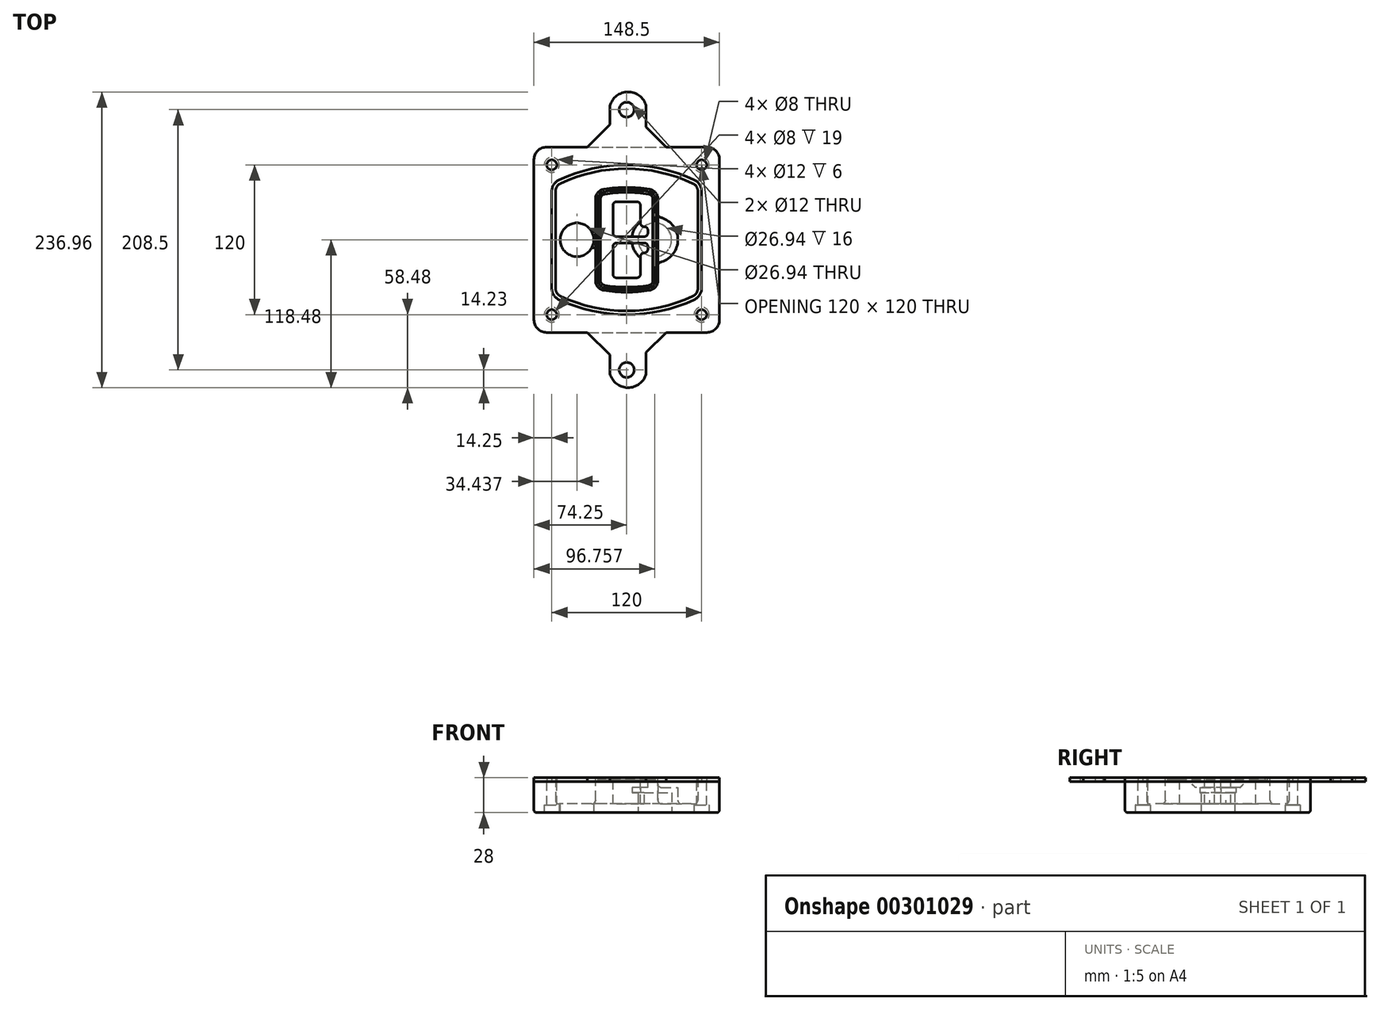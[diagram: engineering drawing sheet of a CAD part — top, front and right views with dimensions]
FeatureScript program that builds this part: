
annotation { "Feature Type Name" : "Feature", "Feature Type Description" : "" }
export const myFeature = defineFeature(function(context is Context, id is Id, definition is map)
    precondition{}
    {
        {
            var Q0;
            Q0=qCreatedBy(makeId("Top.planeOp"),FACE);
            var sketch = newSketch(context, id + "F0", { "sketchPlane" : qUnion([Q0])});
            skPoint(sketch, "E0.rect.middle", {"position": v(0, 0) * mm});
            skLineSegment(sketch, "E1.bottom", {"start": v(-64.25, -74.25) * mm, "end": v(64.25, -74.25) * mm});
            skLineSegment(sketch, "E1.top", {"start": v(-64.25, 74.25) * mm, "end": v(64.25, 74.25) * mm});
            skLineSegment(sketch, "E1.left", {"start": v(-74.25, -64.25) * mm, "end": v(-74.25, 64.25) * mm});
            skLineSegment(sketch, "E1.right", {"start": v(74.25, -64.25) * mm, "end": v(74.25, 64.25) * mm});
            skLineSegment(sketch, "E2", {"start": v(-74.25, 74.25) * mm, "end": v(74.25, -74.25) * mm, "construction": true});
            skLineSegment(sketch, "E3", {"start": v(74.25, 74.25) * mm, "end": v(-74.25, -74.25) * mm, "construction": true});
            skCircle(sketch, "E4", {"center": v(-60, 60) * mm, "radius": 4 * mm});
            skCircle(sketch, "E5", {"center": v(60, 60) * mm, "radius": 4 * mm});
            skCircle(sketch, "E6", {"center": v(60, -60) * mm, "radius": 4 * mm});
            skCircle(sketch, "E7", {"center": v(-60, -60) * mm, "radius": 4 * mm});
            skLineSegment(sketch, "E8", {"start": v(-60, 60) * mm, "end": v(60, 60) * mm, "construction": true});
            skLineSegment(sketch, "E9", {"start": v(60, 60) * mm, "end": v(60, -60) * mm, "construction": true});
            skLineSegment(sketch, "E10", {"start": v(60, -60) * mm, "end": v(-60, -60) * mm, "construction": true});
            skLineSegment(sketch, "E11", {"start": v(-60, -60) * mm, "end": v(-60, 60) * mm, "construction": true});
            skLineSegment(sketch, "E12", {"start": v(-60, 38.83) * mm, "end": v(-60, -38.83) * mm});
            skLineSegment(sketch, "E13", {"start": v(60, 38.83) * mm, "end": v(60, -38.83) * mm});
            skArc(sketch, "E14", {"start": v(54.26, 47.88) * mm, "mid": v(0, 60) * mm, "end": v(-54.26, 47.88) * mm});
            skArc(sketch, "E15", {"start": v(-54.26, -47.88) * mm, "mid": v(0, -60) * mm, "end": v(54.26, -47.88) * mm});
            skLineSegment(sketch, "E16", {"start": v(-60, 0) * mm, "end": v(60, 0) * mm, "construction": true});
            skPoint(sketch, "E17.visualSharp", {"position": v(-60, -45) * mm});
            skArc(sketch, "E17.filletArc", {"start": v(-60, -38.83) * mm, "mid": v(-58.44, -44.2) * mm, "end": v(-54.26, -47.88) * mm});
            skPoint(sketch, "E18.visualSharp", {"position": v(-60, 45) * mm});
            skArc(sketch, "E18.filletArc", {"start": v(-54.26, 47.88) * mm, "mid": v(-58.44, 44.2) * mm, "end": v(-60, 38.83) * mm});
            skPoint(sketch, "E19.visualSharp", {"position": v(60, 45) * mm});
            skArc(sketch, "E19.filletArc", {"start": v(60, 38.83) * mm, "mid": v(58.44, 44.2) * mm, "end": v(54.26, 47.88) * mm});
            skPoint(sketch, "E20.visualSharp", {"position": v(60, -45) * mm});
            skArc(sketch, "E20.filletArc", {"start": v(54.26, -47.88) * mm, "mid": v(58.44, -44.2) * mm, "end": v(60, -38.83) * mm});
            skPoint(sketch, "E21.visualSharp", {"position": v(-74.25, 74.25) * mm});
            skArc(sketch, "E21.filletArc", {"start": v(-64.25, 74.25) * mm, "mid": v(-71.32, 71.32) * mm, "end": v(-74.25, 64.25) * mm});
            skPoint(sketch, "E22.visualSharp", {"position": v(74.25, 74.25) * mm});
            skArc(sketch, "E22.filletArc", {"start": v(74.25, 64.25) * mm, "mid": v(71.32, 71.32) * mm, "end": v(64.25, 74.25) * mm});
            skPoint(sketch, "E23.visualSharp", {"position": v(74.25, -74.25) * mm});
            skArc(sketch, "E23.filletArc", {"start": v(64.25, -74.25) * mm, "mid": v(71.32, -71.32) * mm, "end": v(74.25, -64.25) * mm});
            skPoint(sketch, "E24.visualSharp", {"position": v(-74.25, -74.25) * mm});
            skArc(sketch, "E24.filletArc", {"start": v(-74.25, -64.25) * mm, "mid": v(-71.32, -71.32) * mm, "end": v(-64.25, -74.25) * mm});
            skArc(sketch, "E25.0", {"start": v(57, 38.83) * mm, "mid": v(55.9, 42.58) * mm, "end": v(52.98, 45.17) * mm});
            skLineSegment(sketch, "E25.1", {"start": v(57, 38.83) * mm, "end": v(57, -38.83) * mm});
            skArc(sketch, "E25.2", {"start": v(52.98, -45.17) * mm, "mid": v(55.9, -42.58) * mm, "end": v(57, -38.83) * mm});
            skArc(sketch, "E25.3", {"start": v(-52.98, -45.17) * mm, "mid": v(0, -57) * mm, "end": v(52.98, -45.17) * mm});
            skArc(sketch, "E25.4", {"start": v(-57, -38.83) * mm, "mid": v(-55.9, -42.58) * mm, "end": v(-52.98, -45.17) * mm});
            skArc(sketch, "E25.5", {"start": v(52.98, 45.17) * mm, "mid": v(0, 57) * mm, "end": v(-52.98, 45.17) * mm});
            skLineSegment(sketch, "E25.6", {"start": v(-57, 38.83) * mm, "end": v(-57, -38.83) * mm});
            skArc(sketch, "E25.7", {"start": v(-52.98, 45.17) * mm, "mid": v(-55.9, 42.58) * mm, "end": v(-57, 38.83) * mm});
            skArc(sketch, "E26.0", {"start": v(-55.96, 51.5) * mm, "mid": v(-61.82, 46.33) * mm, "end": v(-64, 38.83) * mm});
            skArc(sketch, "E26.1", {"start": v(55.96, 51.5) * mm, "mid": v(0, 64) * mm, "end": v(-55.96, 51.5) * mm});
            skArc(sketch, "E26.2", {"start": v(64, 38.83) * mm, "mid": v(61.82, 46.33) * mm, "end": v(55.96, 51.5) * mm});
            skLineSegment(sketch, "E26.3", {"start": v(64, 38.83) * mm, "end": v(64, -38.83) * mm});
            skArc(sketch, "E26.4", {"start": v(55.96, -51.5) * mm, "mid": v(61.82, -46.33) * mm, "end": v(64, -38.83) * mm});
            skLineSegment(sketch, "E26.5", {"start": v(-64, 38.83) * mm, "end": v(-64, -38.83) * mm});
            skArc(sketch, "E26.6", {"start": v(-55.96, -51.5) * mm, "mid": v(0, -64) * mm, "end": v(55.96, -51.5) * mm});
            skArc(sketch, "E26.7", {"start": v(-64, -38.83) * mm, "mid": v(-61.82, -46.33) * mm, "end": v(-55.96, -51.5) * mm});
            skSolve(sketch);
        }
        {
            var Q0;
            Q0=makeQuery(id+"F0.imprint","IMPRINT",FACE,{"disambiguationData":[TD([[makeQuery(id+"F0.imprint","IMPRINT",EDGE,{"derivedFrom":sQuery(id+"F0.wireOp",EDGE,"E1.bottom")}),1.0]])]});
            var Q1;
            Q1=makeQuery(id+"F0.imprint","IMPRINT",FACE,{"disambiguationData":[TD([[makeQuery(id+"F0.imprint","IMPRINT",EDGE,{"derivedFrom":sQuery(id+"F0.wireOp",EDGE,"E12")}),1.0]])]});
            var Q2;
            Q2=makeQuery(id+"F0.imprint","IMPRINT",FACE,{"disambiguationData":[TD([[makeQuery(id+"F0.imprint","IMPRINT",EDGE,{"derivedFrom":sQuery(id+"F0.wireOp",EDGE,"E25.0")}),1.0]])]});
            var Q3;
            Q3=makeQuery(id+"F0.imprint","IMPRINT",FACE,{"disambiguationData":[TD([[makeQuery(id+"F0.imprint","IMPRINT",EDGE,{"derivedFrom":sQuery(id+"F0.wireOp",EDGE,"E12")}),-1.0]])]});
            extrude(context, id + "F1", {"entities" : qUnion([Q0, Q1, Q2, Q3]), "oppositeDirection" : true, "depth" : 25 * mm});
        }
        {
            var Q0;
            Q0=makeQuery(id+"F0.imprint","IMPRINT",FACE,{"disambiguationData":[TD([[makeQuery(id+"F0.imprint","IMPRINT",EDGE,{"derivedFrom":sQuery(id+"F0.wireOp",EDGE,"E12")}),1.0]])]});
            extrude(context, id + "F2", {"entities" : qUnion([Q0]), "operationType" : NewBodyOperationType.ADD, "depth" : 3 * mm});
        }
        {
            var Q0;
            Q0=makeQuery(id+"F0.imprint","IMPRINT",FACE,{"disambiguationData":[TD([[makeQuery(id+"F0.imprint","IMPRINT",EDGE,{"derivedFrom":sQuery(id+"F0.wireOp",EDGE,"E25.0")}),1.0]])]});
            extrude(context, id + "F3", {"entities" : qUnion([Q0]), "operationType" : NewBodyOperationType.REMOVE, "oppositeDirection" : true, "depth" : 18 * mm});
        }
        {
            var Q0;
            Q0=makeQuery(id+"F2.opExtrude","CAP_FACE",FACE,{"disambiguationData":[OSD([sQuery(id+"F0.wireOp",EDGE,"E12"),sQuery(id+"F0.wireOp",EDGE,"E13"),sQuery(id+"F0.wireOp",EDGE,"E14"),sQuery(id+"F0.wireOp",EDGE,"E15"),sQuery(id+"F0.wireOp",EDGE,"E17.filletArc"),sQuery(id+"F0.wireOp",EDGE,"E18.filletArc"),sQuery(id+"F0.wireOp",EDGE,"E19.filletArc"),sQuery(id+"F0.wireOp",EDGE,"E20.filletArc"),sQuery(id+"F0.wireOp",EDGE,"E25.0"),sQuery(id+"F0.wireOp",EDGE,"E25.1"),sQuery(id+"F0.wireOp",EDGE,"E25.2"),sQuery(id+"F0.wireOp",EDGE,"E25.3"),sQuery(id+"F0.wireOp",EDGE,"E25.4"),sQuery(id+"F0.wireOp",EDGE,"E25.5"),sQuery(id+"F0.wireOp",EDGE,"E25.6"),sQuery(id+"F0.wireOp",EDGE,"E25.7")])],"isStart":false});
            var sketch = newSketch(context, id + "F4", { "sketchPlane" : qUnion([Q0])});
            skArc(sketch, "E27.0", {"start": v(-18.34, -40.45) * mm, "mid": v(0, -42) * mm, "end": v(18.34, -40.45) * mm});
            skArc(sketch, "E28.0", {"start": v(18.34, 40.45) * mm, "mid": v(0, 42) * mm, "end": v(-18.34, 40.45) * mm});
            skLineSegment(sketch, "E29", {"start": v(-25, 32.57) * mm, "end": v(-25, -32.57) * mm});
            skLineSegment(sketch, "E30", {"start": v(25, 32.57) * mm, "end": v(25, -32.57) * mm});
            skLineSegment(sketch, "E31", {"start": v(-25, 39.1) * mm, "end": v(25, 39.1) * mm, "construction": true});
            skLineSegment(sketch, "E32", {"start": v(-25, -39.1) * mm, "end": v(25, -39.1) * mm, "construction": true});
            skPoint(sketch, "E33.visualSharp", {"position": v(-25, 39.1) * mm});
            skArc(sketch, "E33.filletArc", {"start": v(-18.34, 40.45) * mm, "mid": v(-23.11, 37.73) * mm, "end": v(-25, 32.57) * mm});
            skPoint(sketch, "E34.visualSharp", {"position": v(25, 39.1) * mm});
            skArc(sketch, "E34.filletArc", {"start": v(25, 32.57) * mm, "mid": v(23.11, 37.73) * mm, "end": v(18.34, 40.45) * mm});
            skPoint(sketch, "E35.visualSharp", {"position": v(25, -39.1) * mm});
            skArc(sketch, "E35.filletArc", {"start": v(18.34, -40.45) * mm, "mid": v(23.11, -37.73) * mm, "end": v(25, -32.57) * mm});
            skPoint(sketch, "E36.visualSharp", {"position": v(-25, -39.1) * mm});
            skArc(sketch, "E36.filletArc", {"start": v(-25, -32.57) * mm, "mid": v(-23.11, -37.73) * mm, "end": v(-18.34, -40.45) * mm});
            skArc(sketch, "E37.0", {"start": v(52.98, 45.17) * mm, "mid": v(0, 57) * mm, "end": v(-52.98, 45.17) * mm});
            skArc(sketch, "E37.1", {"start": v(-52.98, 45.17) * mm, "mid": v(-55.9, 42.58) * mm, "end": v(-57, 38.83) * mm});
            skLineSegment(sketch, "E37.2", {"start": v(-57, 38.83) * mm, "end": v(-57, -38.83) * mm});
            skArc(sketch, "E37.3", {"start": v(-57, -38.83) * mm, "mid": v(-55.9, -42.58) * mm, "end": v(-52.98, -45.17) * mm});
            skArc(sketch, "E37.4", {"start": v(-52.98, -45.17) * mm, "mid": v(0, -57) * mm, "end": v(52.98, -45.17) * mm});
            skArc(sketch, "E37.5", {"start": v(52.98, -45.17) * mm, "mid": v(55.9, -42.58) * mm, "end": v(57, -38.83) * mm});
            skLineSegment(sketch, "E37.6", {"start": v(57, 38.83) * mm, "end": v(57, -38.83) * mm});
            skArc(sketch, "E37.7", {"start": v(57, 38.83) * mm, "mid": v(55.9, 42.58) * mm, "end": v(52.98, 45.17) * mm});
            skLineSegment(sketch, "E38.0", {"start": v(23, 32.57) * mm, "end": v(23, -32.57) * mm});
            skArc(sketch, "E38.1", {"start": v(18, -38.48) * mm, "mid": v(21.58, -36.44) * mm, "end": v(23, -32.57) * mm});
            skArc(sketch, "E38.2", {"start": v(-18, -38.48) * mm, "mid": v(0, -40) * mm, "end": v(18, -38.48) * mm});
            skArc(sketch, "E38.3", {"start": v(-23, -32.57) * mm, "mid": v(-21.58, -36.44) * mm, "end": v(-18, -38.48) * mm});
            skLineSegment(sketch, "E38.4", {"start": v(-23, 32.57) * mm, "end": v(-23, -32.57) * mm});
            skArc(sketch, "E38.5", {"start": v(23, 32.57) * mm, "mid": v(21.58, 36.44) * mm, "end": v(18, 38.48) * mm});
            skArc(sketch, "E38.6", {"start": v(-18, 38.48) * mm, "mid": v(-21.58, 36.44) * mm, "end": v(-23, 32.57) * mm});
            skArc(sketch, "E38.7", {"start": v(18, 38.48) * mm, "mid": v(0, 40) * mm, "end": v(-18, 38.48) * mm});
            skArc(sketch, "E39.0", {"start": v(21, 32.57) * mm, "mid": v(20.06, 35.15) * mm, "end": v(17.67, 36.5) * mm});
            skLineSegment(sketch, "E39.1", {"start": v(21, 32.57) * mm, "end": v(21, -32.57) * mm});
            skArc(sketch, "E39.2", {"start": v(17.67, -36.5) * mm, "mid": v(20.06, -35.15) * mm, "end": v(21, -32.57) * mm});
            skArc(sketch, "E39.3", {"start": v(-17.67, -36.5) * mm, "mid": v(0, -38) * mm, "end": v(17.67, -36.5) * mm});
            skArc(sketch, "E39.4", {"start": v(-21, -32.57) * mm, "mid": v(-20.06, -35.15) * mm, "end": v(-17.67, -36.5) * mm});
            skArc(sketch, "E39.5", {"start": v(17.67, 36.5) * mm, "mid": v(0, 38) * mm, "end": v(-17.67, 36.5) * mm});
            skLineSegment(sketch, "E39.6", {"start": v(-21, 32.57) * mm, "end": v(-21, -32.57) * mm});
            skArc(sketch, "E39.7", {"start": v(-17.67, 36.5) * mm, "mid": v(-20.06, 35.15) * mm, "end": v(-21, 32.57) * mm});
            skLineSegment(sketch, "E40", {"start": v(-25, 0) * mm, "end": v(25, 0) * mm, "construction": true});
            skLineSegment(sketch, "E41", {"start": v(-11, 5.5) * mm, "end": v(-11, 27.5) * mm});
            skLineSegment(sketch, "E42", {"start": v(-8, 30.5) * mm, "end": v(8, 30.5) * mm});
            skLineSegment(sketch, "E43", {"start": v(11, 27.5) * mm, "end": v(11, 13.5) * mm});
            skLineSegment(sketch, "E44", {"start": v(14, 10.5) * mm, "end": v(14, 10.5) * mm});
            skLineSegment(sketch, "E45", {"start": v(17, 7.5) * mm, "end": v(17, 5.5) * mm});
            skLineSegment(sketch, "E46", {"start": v(14, 2.5) * mm, "end": v(-8, 2.5) * mm});
            skPoint(sketch, "E47.visualSharp", {"position": v(-11, 30.5) * mm});
            skArc(sketch, "E47.filletArc", {"start": v(-8, 30.5) * mm, "mid": v(-10.12, 29.62) * mm, "end": v(-11, 27.5) * mm});
            skPoint(sketch, "E48.visualSharp", {"position": v(11, 30.5) * mm});
            skArc(sketch, "E48.filletArc", {"start": v(11, 27.5) * mm, "mid": v(10.12, 29.62) * mm, "end": v(8, 30.5) * mm});
            skPoint(sketch, "E49.visualSharp", {"position": v(11, 10.5) * mm});
            skArc(sketch, "E49.filletArc", {"start": v(11, 13.5) * mm, "mid": v(11.88, 11.38) * mm, "end": v(14, 10.5) * mm});
            skPoint(sketch, "E50.visualSharp", {"position": v(17, 10.5) * mm});
            skArc(sketch, "E50.filletArc", {"start": v(17, 7.5) * mm, "mid": v(16.12, 9.62) * mm, "end": v(14, 10.5) * mm});
            skPoint(sketch, "E51.visualSharp", {"position": v(17, 2.5) * mm});
            skArc(sketch, "E51.filletArc", {"start": v(14, 2.5) * mm, "mid": v(16.12, 3.38) * mm, "end": v(17, 5.5) * mm});
            skPoint(sketch, "E52.visualSharp", {"position": v(-11, 2.5) * mm});
            skArc(sketch, "E52.filletArc", {"start": v(-11, 5.5) * mm, "mid": v(-10.12, 3.38) * mm, "end": v(-8, 2.5) * mm});
            skLineSegment(sketch, "E53.0.MirrorCS", {"start": v(14, -2.5) * mm, "end": v(-8, -2.5) * mm});
            skArc(sketch, "E54.0.MirrorCS", {"start": v(-11, -5.5) * mm, "mid": v(-10.12, -3.38) * mm, "end": v(-8, -2.5) * mm});
            skLineSegment(sketch, "E55.0.MirrorCS", {"start": v(-11, -5.5) * mm, "end": v(-11, -27.5) * mm});
            skArc(sketch, "E56.0.MirrorCS", {"start": v(-8, -30.5) * mm, "mid": v(-10.12, -29.62) * mm, "end": v(-11, -27.5) * mm});
            skLineSegment(sketch, "E57.0.MirrorCS", {"start": v(-8, -30.5) * mm, "end": v(8, -30.5) * mm});
            skArc(sketch, "E58.0.MirrorCS", {"start": v(11, -27.5) * mm, "mid": v(10.12, -29.62) * mm, "end": v(8, -30.5) * mm});
            skLineSegment(sketch, "E59.0.MirrorCS", {"start": v(11, -27.5) * mm, "end": v(11, -13.5) * mm});
            skArc(sketch, "E60.0.MirrorCS", {"start": v(11, -13.5) * mm, "mid": v(11.88, -11.38) * mm, "end": v(14, -10.5) * mm});
            skArc(sketch, "E61.0.MirrorCS", {"start": v(17, -7.5) * mm, "mid": v(16.12, -9.62) * mm, "end": v(14, -10.5) * mm});
            skLineSegment(sketch, "E62.0.MirrorCS", {"start": v(17, -7.5) * mm, "end": v(17, -5.5) * mm});
            skArc(sketch, "E63.0.MirrorCS", {"start": v(14, -2.5) * mm, "mid": v(16.12, -3.38) * mm, "end": v(17, -5.5) * mm});
            skSolve(sketch);
        }
        {
            var Q0;
            Q0=makeQuery(id+"F4.imprint","IMPRINT",FACE,{"disambiguationData":[TD([[makeQuery(id+"F4.imprint","IMPRINT",EDGE,{"derivedFrom":sQuery(id+"F4.wireOp",EDGE,"E27.0")}),1.0]])]});
            var Q1;
            Q1=makeQuery(id+"F4.imprint","IMPRINT",FACE,{"disambiguationData":[TD([[makeQuery(id+"F4.imprint","IMPRINT",EDGE,{"derivedFrom":sQuery(id+"F4.wireOp",EDGE,"E38.0")}),-1.0]])]});
            var Q2;
            Q2=makeQuery(id+"F4.imprint","IMPRINT",FACE,{"disambiguationData":[TD([[makeQuery(id+"F4.imprint","IMPRINT",EDGE,{"derivedFrom":sQuery(id+"F4.wireOp",EDGE,"E39.0")}),1.0]])]});
            extrude(context, id + "F5", {"entities" : qUnion([Q0, Q1, Q2]), "operationType" : NewBodyOperationType.ADD, "endBound" : BoundingType.UP_TO_NEXT, "oppositeDirection" : true, "depth" : 25 * mm});
        }
        {
            var Q0;
            Q0=makeQuery(id+"F4.imprint","IMPRINT",FACE,{"disambiguationData":[TD([[makeQuery(id+"F4.imprint","IMPRINT",EDGE,{"derivedFrom":sQuery(id+"F4.wireOp",EDGE,"E38.0")}),-1.0]])]});
            extrude(context, id + "F6", {"entities" : qUnion([Q0]), "operationType" : NewBodyOperationType.REMOVE, "oppositeDirection" : true, "depth" : 2 * mm});
        }
        {
            var Q0;
            Q0=makeQuery(id+"F1.opExtrude","CAP_FACE",FACE,{"disambiguationData":[OSD([sQuery(id+"F0.wireOp",EDGE,"E1.bottom"),sQuery(id+"F0.wireOp",EDGE,"E1.top"),sQuery(id+"F0.wireOp",EDGE,"E1.left"),sQuery(id+"F0.wireOp",EDGE,"E1.right"),sQuery(id+"F0.wireOp",EDGE,"E4"),sQuery(id+"F0.wireOp",EDGE,"E5"),sQuery(id+"F0.wireOp",EDGE,"E6"),sQuery(id+"F0.wireOp",EDGE,"E7"),sQuery(id+"F0.wireOp",EDGE,"E21.filletArc"),sQuery(id+"F0.wireOp",EDGE,"E22.filletArc"),sQuery(id+"F0.wireOp",EDGE,"E23.filletArc"),sQuery(id+"F0.wireOp",EDGE,"E24.filletArc")])],"isStart":false});
            var sketch = newSketch(context, id + "F7", { "sketchPlane" : qUnion([Q0])});
            skCircle(sketch, "E64", {"center": v(22.5, 0) * mm, "radius": 13.47 * mm});
            skCircle(sketch, "E65", {"center": v(-39.81, 0) * mm, "radius": 13.47 * mm});
            skLineSegment(sketch, "E66", {"start": v(74.25, 0) * mm, "end": v(-74.25, 0) * mm});
            skCircle(sketch, "E67", {"center": v(22.5, 0) * mm, "radius": 18.47 * mm});
            skCircle(sketch, "E68", {"center": v(60, -60) * mm, "radius": 6 * mm});
            skCircle(sketch, "E69", {"center": v(-60, -60) * mm, "radius": 6 * mm});
            skCircle(sketch, "E70", {"center": v(-60, 60) * mm, "radius": 6 * mm});
            skCircle(sketch, "E71", {"center": v(60, 60) * mm, "radius": 6 * mm});
            skSolve(sketch);
        }
        {
            var Q0;
            {var subQ1=sQuery(id+"F7.wireOp",EDGE,"E66");var subQ4=sQuery(id+"F7.wireOp",EDGE,"E64");var subQ6=makeQuery(id+"F7.imprint","INTERSECT",VERTEX,{"disambiguationData":[OD(0.0)],"derivedFrom":[subQ4,subQ1]});Q0=makeQuery(id+"F7.imprint","IMPRINT",FACE,{"disambiguationData":[TD([[makeQuery(id+"F7.imprint","IMPRINT",EDGE,{"disambiguationData":[TD([[subQ6,-1.0]])],"derivedFrom":subQ4}),-1.0]])]});}
            var Q1;
            {var subQ0=sQuery(id+"F7.wireOp",EDGE,"E66");var subQ1=sQuery(id+"F7.wireOp",EDGE,"E64");var subQ3=makeQuery(id+"F7.imprint","INTERSECT",VERTEX,{"disambiguationData":[OD(0.0)],"derivedFrom":[subQ1,subQ0]});Q1=makeQuery(id+"F7.imprint","IMPRINT",FACE,{"disambiguationData":[TD([[makeQuery(id+"F7.imprint","IMPRINT",EDGE,{"disambiguationData":[TD([[subQ3,-1.0]])],"derivedFrom":subQ1}),1.0]])]});}
            var Q2;
            {var subQ0=sQuery(id+"F7.wireOp",EDGE,"E66");var subQ1=sQuery(id+"F7.wireOp",EDGE,"E64");var subQ3=makeQuery(id+"F7.imprint","INTERSECT",VERTEX,{"disambiguationData":[OD(0.0)],"derivedFrom":[subQ1,subQ0]});Q2=makeQuery(id+"F7.imprint","IMPRINT",FACE,{"disambiguationData":[TD([[makeQuery(id+"F7.imprint","IMPRINT",EDGE,{"disambiguationData":[TD([[subQ3,1.0]])],"derivedFrom":subQ1}),1.0]])]});}
            var Q3;
            {var subQ1=sQuery(id+"F7.wireOp",EDGE,"E66");var subQ4=sQuery(id+"F7.wireOp",EDGE,"E64");var subQ6=makeQuery(id+"F7.imprint","INTERSECT",VERTEX,{"disambiguationData":[OD(0.0)],"derivedFrom":[subQ4,subQ1]});Q3=makeQuery(id+"F7.imprint","IMPRINT",FACE,{"disambiguationData":[TD([[makeQuery(id+"F7.imprint","IMPRINT",EDGE,{"disambiguationData":[TD([[subQ6,1.0]])],"derivedFrom":subQ4}),-1.0]])]});}
            extrude(context, id + "F8", {"entities" : qUnion([Q0, Q1, Q2, Q3]), "operationType" : NewBodyOperationType.ADD, "oppositeDirection" : true, "depth" : 20 * mm});
        }
        {
            var Q0;
            {var subQ0=sQuery(id+"F7.wireOp",EDGE,"E66");var subQ1=sQuery(id+"F7.wireOp",EDGE,"E64");var subQ3=makeQuery(id+"F7.imprint","INTERSECT",VERTEX,{"disambiguationData":[OD(0.0)],"derivedFrom":[subQ1,subQ0]});Q0=makeQuery(id+"F7.imprint","IMPRINT",FACE,{"disambiguationData":[TD([[makeQuery(id+"F7.imprint","IMPRINT",EDGE,{"disambiguationData":[TD([[subQ3,-1.0]])],"derivedFrom":subQ1}),1.0]])]});}
            var Q1;
            {var subQ0=sQuery(id+"F7.wireOp",EDGE,"E66");var subQ1=sQuery(id+"F7.wireOp",EDGE,"E64");var subQ3=makeQuery(id+"F7.imprint","INTERSECT",VERTEX,{"disambiguationData":[OD(0.0)],"derivedFrom":[subQ1,subQ0]});Q1=makeQuery(id+"F7.imprint","IMPRINT",FACE,{"disambiguationData":[TD([[makeQuery(id+"F7.imprint","IMPRINT",EDGE,{"disambiguationData":[TD([[subQ3,1.0]])],"derivedFrom":subQ1}),1.0]])]});}
            extrude(context, id + "F9", {"entities" : qUnion([Q0, Q1]), "operationType" : NewBodyOperationType.REMOVE, "oppositeDirection" : true, "depth" : 16 * mm});
        }
        {
            var Q0;
            {var subQ0=sQuery(id+"F7.wireOp",EDGE,"E66");var subQ1=sQuery(id+"F7.wireOp",EDGE,"E65");var subQ3=makeQuery(id+"F7.imprint","INTERSECT",VERTEX,{"disambiguationData":[OD(0.0)],"derivedFrom":[subQ1,subQ0]});Q0=makeQuery(id+"F7.imprint","IMPRINT",FACE,{"disambiguationData":[TD([[makeQuery(id+"F7.imprint","IMPRINT",EDGE,{"disambiguationData":[TD([[subQ3,-1.0]])],"derivedFrom":subQ1}),1.0]])]});}
            var Q1;
            {var subQ0=sQuery(id+"F7.wireOp",EDGE,"E66");var subQ1=sQuery(id+"F7.wireOp",EDGE,"E65");var subQ3=makeQuery(id+"F7.imprint","INTERSECT",VERTEX,{"disambiguationData":[OD(0.0)],"derivedFrom":[subQ1,subQ0]});Q1=makeQuery(id+"F7.imprint","IMPRINT",FACE,{"disambiguationData":[TD([[makeQuery(id+"F7.imprint","IMPRINT",EDGE,{"disambiguationData":[TD([[subQ3,1.0]])],"derivedFrom":subQ1}),1.0]])]});}
            extrude(context, id + "F10", {"entities" : qUnion([Q0, Q1]), "operationType" : NewBodyOperationType.REMOVE, "oppositeDirection" : true, "depth" : 25 * mm});
        }
        {
            var Q0;
            Q0=makeQuery(id+"F7.imprint","IMPRINT",FACE,{"disambiguationData":[TD([[makeQuery(id+"F7.imprint","IMPRINT",EDGE,{"derivedFrom":sQuery(id+"F7.wireOp",EDGE,"E68")}),1.0]])]});
            var Q1;
            Q1=makeQuery(id+"F7.imprint","IMPRINT",FACE,{"disambiguationData":[TD([[makeQuery(id+"F7.imprint","IMPRINT",EDGE,{"derivedFrom":makeQuery(id+"F1.opExtrude","CAP_EDGE",EDGE,{"disambiguationData":[OSD([sQuery(id+"F0.wireOp",EDGE,"E5")])],"isStart":false})}),-1.0]])]});
            var Q2;
            Q2=makeQuery(id+"F7.imprint","IMPRINT",FACE,{"disambiguationData":[TD([[makeQuery(id+"F7.imprint","IMPRINT",EDGE,{"derivedFrom":sQuery(id+"F7.wireOp",EDGE,"E69")}),1.0]])]});
            var Q3;
            Q3=makeQuery(id+"F7.imprint","IMPRINT",FACE,{"disambiguationData":[TD([[makeQuery(id+"F7.imprint","IMPRINT",EDGE,{"derivedFrom":makeQuery(id+"F1.opExtrude","CAP_EDGE",EDGE,{"disambiguationData":[OSD([sQuery(id+"F0.wireOp",EDGE,"E4")])],"isStart":false})}),-1.0]])]});
            var Q4;
            Q4=makeQuery(id+"F7.imprint","IMPRINT",FACE,{"disambiguationData":[TD([[makeQuery(id+"F7.imprint","IMPRINT",EDGE,{"derivedFrom":sQuery(id+"F7.wireOp",EDGE,"E70")}),1.0]])]});
            var Q5;
            Q5=makeQuery(id+"F7.imprint","IMPRINT",FACE,{"disambiguationData":[TD([[makeQuery(id+"F7.imprint","IMPRINT",EDGE,{"derivedFrom":makeQuery(id+"F1.opExtrude","CAP_EDGE",EDGE,{"disambiguationData":[OSD([sQuery(id+"F0.wireOp",EDGE,"E7")])],"isStart":false})}),-1.0]])]});
            var Q6;
            Q6=makeQuery(id+"F7.imprint","IMPRINT",FACE,{"disambiguationData":[TD([[makeQuery(id+"F7.imprint","IMPRINT",EDGE,{"derivedFrom":sQuery(id+"F7.wireOp",EDGE,"E71")}),1.0]])]});
            var Q7;
            Q7=makeQuery(id+"F7.imprint","IMPRINT",FACE,{"disambiguationData":[TD([[makeQuery(id+"F7.imprint","IMPRINT",EDGE,{"derivedFrom":makeQuery(id+"F1.opExtrude","CAP_EDGE",EDGE,{"disambiguationData":[OSD([sQuery(id+"F0.wireOp",EDGE,"E6")])],"isStart":false})}),-1.0]])]});
            extrude(context, id + "F11", {"entities" : qUnion([Q0, Q1, Q2, Q3, Q4, Q5, Q6, Q7]), "operationType" : NewBodyOperationType.REMOVE, "oppositeDirection" : true, "depth" : 6 * mm});
        }
        {
            var Q0;
            Q0=makeQuery(id+"F9.boolean.opBoolean","COPY",FACE,{"derivedFrom":makeQuery(id+"F9.opExtrude","CAP_FACE",FACE,{"disambiguationData":[OSD([sQuery(id+"F7.wireOp",EDGE,"E64")])],"isStart":false})});
            var sketch = newSketch(context, id + "F12", { "sketchPlane" : qUnion([Q0])});
            skArc(sketch, "E72.0", {"start": v(11, 14.45) * mm, "mid": v(6.45, 9.13) * mm, "end": v(4.2, 2.5) * mm});
            skArc(sketch, "E72.1", {"start": v(4.2, -2.5) * mm, "mid": v(6.45, -9.13) * mm, "end": v(11, -14.45) * mm});
            skLineSegment(sketch, "E73", {"start": v(4.2, -2.5) * mm, "end": v(14, -2.5) * mm});
            skLineSegment(sketch, "E74.0", {"start": v(14, 2.5) * mm, "end": v(4.2, 2.5) * mm});
            skArc(sketch, "E74.1", {"start": v(14, 2.5) * mm, "mid": v(16.12, 3.38) * mm, "end": v(17, 5.5) * mm});
            skLineSegment(sketch, "E74.2", {"start": v(17, 7.5) * mm, "end": v(17, 5.5) * mm});
            skArc(sketch, "E74.3", {"start": v(17, 7.5) * mm, "mid": v(16.12, 9.62) * mm, "end": v(14, 10.5) * mm});
            skArc(sketch, "E74.4", {"start": v(11, 13.5) * mm, "mid": v(11.88, 11.38) * mm, "end": v(14, 10.5) * mm});
            skLineSegment(sketch, "E74.5", {"start": v(11, 14.45) * mm, "end": v(11, 13.5) * mm});
            skLineSegment(sketch, "E74.7", {"start": v(14, -2.5) * mm, "end": v(4.2, -2.5) * mm});
            skArc(sketch, "E74.8", {"start": v(14, -2.5) * mm, "mid": v(16.12, -3.38) * mm, "end": v(17, -5.5) * mm});
            skLineSegment(sketch, "E74.9", {"start": v(17, -7.5) * mm, "end": v(17, -5.5) * mm});
            skArc(sketch, "E74.10", {"start": v(17, -7.5) * mm, "mid": v(16.12, -9.62) * mm, "end": v(14, -10.5) * mm});
            skArc(sketch, "E74.11", {"start": v(11, -13.5) * mm, "mid": v(11.88, -11.38) * mm, "end": v(14, -10.5) * mm});
            skLineSegment(sketch, "E74.12", {"start": v(11, -14.45) * mm, "end": v(11, -13.5) * mm});
            skPoint(sketch, "E75.orphan", {"position": v(11, -27.5) * mm});
            skPoint(sketch, "E76.orphan", {"position": v(-8, -2.5) * mm});
            skPoint(sketch, "E77.orphan", {"position": v(-8, 2.5) * mm});
            skPoint(sketch, "E78.orphan", {"position": v(11, 27.5) * mm});
            skSolve(sketch);
        }
        {
            var Q0;
            {var subQ7=sQuery(id+"F12.wireOp",EDGE,"E72.0");var subQ14=sQuery(id+"F12.wireOp",EDGE,"E72.1");var subQ16=sQuery(id+"F12.wireOp",EDGE,"E74.1");var subQ18=sQuery(id+"F12.wireOp",EDGE,"E74.8");Q0=qUnion([makeQuery(id+"F12.imprint","IMPRINT",FACE,{"disambiguationData":[TD([[makeQuery(id+"F12.imprint","IMPRINT",EDGE,{"derivedFrom":subQ7}),1.0]])]}),makeQuery(id+"F12.imprint","IMPRINT",FACE,{"disambiguationData":[TD([[makeQuery(id+"F12.imprint","IMPRINT",EDGE,{"derivedFrom":subQ14}),1.0]])]}),makeQuery(id+"F12.imprint","IMPRINT",FACE,{"disambiguationData":[TD([[makeQuery(id+"F12.imprint","IMPRINT",EDGE,{"derivedFrom":subQ16}),1.0]])]}),makeQuery(id+"F12.imprint","IMPRINT",FACE,{"disambiguationData":[TD([[makeQuery(id+"F12.imprint","IMPRINT",EDGE,{"derivedFrom":subQ18}),-1.0]])]})]);}
            var Q1;
            Q1=makeQuery(id+"F5.boolean.opBoolean","SPLIT",FACE,{"disambiguationData":[TD([makeQuery(id+"F5.opExtrude","SWEPT_FACE",FACE,{"disambiguationData":[OSD([sQuery(id+"F4.wireOp",EDGE,"E41")])]})])],"derivedFrom":makeQuery(id+"F3.boolean.opBoolean","COPY",FACE,{"derivedFrom":makeQuery(id+"F3.opExtrude","CAP_FACE",FACE,{"disambiguationData":[OSD([sQuery(id+"F0.wireOp",EDGE,"E25.0"),sQuery(id+"F0.wireOp",EDGE,"E25.1"),sQuery(id+"F0.wireOp",EDGE,"E25.2"),sQuery(id+"F0.wireOp",EDGE,"E25.3"),sQuery(id+"F0.wireOp",EDGE,"E25.4"),sQuery(id+"F0.wireOp",EDGE,"E25.5"),sQuery(id+"F0.wireOp",EDGE,"E25.6"),sQuery(id+"F0.wireOp",EDGE,"E25.7")])],"isStart":false})})});
            extrude(context, id + "F13", {"entities" : qUnion([Q0]), "operationType" : NewBodyOperationType.REMOVE, "endBound" : BoundingType.UP_TO_SURFACE, "endBoundEntityFace" : qUnion([Q1]), "depth" : 25 * mm});
        }
        {
            var Q0;
            Q0=makeQuery(id+"F3.boolean.opBoolean","COPY",EDGE,{"derivedFrom":makeQuery(id+"F3.opExtrude","CAP_EDGE",EDGE,{"disambiguationData":[OSD([sQuery(id+"F0.wireOp",EDGE,"E25.6")])],"isStart":false})});
            var Q1;
            Q1=makeQuery(id+"F8.boolean.opBoolean","INTERSECT",EDGE,{"derivedFrom":[makeQuery(id+"F5.opExtrude","SWEPT_FACE",FACE,{"disambiguationData":[OSD([sQuery(id+"F4.wireOp",EDGE,"E30")])]}),makeQuery(id+"F8.opExtrude","CAP_FACE",FACE,{"disambiguationData":[OSD([sQuery(id+"F7.wireOp",EDGE,"E67")])],"isStart":false})]});
            var Q2;
            Q2=makeQuery(id+"F8.boolean.opBoolean","INTERSECT",EDGE,{"disambiguationData":[OD(1.0)],"derivedFrom":[makeQuery(id+"F5.opExtrude","SWEPT_FACE",FACE,{"disambiguationData":[OSD([sQuery(id+"F4.wireOp",EDGE,"E30")])]}),makeQuery(id+"F8.opExtrude","SWEPT_FACE",FACE,{"disambiguationData":[OSD([sQuery(id+"F7.wireOp",EDGE,"E67")])]})]});
            var Q3;
            {var subQ0=sQuery(id+"F4.wireOp",EDGE,"E30");Q3=makeQuery(id+"F8.boolean.opBoolean","SPLIT",EDGE,{"disambiguationData":[TD([makeQuery(id+"F5.opExtrude","SWEPT_FACE",FACE,{"disambiguationData":[OSD([sQuery(id+"F4.wireOp",EDGE,"E35.filletArc")])]})])],"derivedFrom":makeQuery(id+"F5.opExtrude","CAP_EDGE",EDGE,{"disambiguationData":[OSD([subQ0])],"isStart":false})});}
            var Q4;
            {var subQ0=sQuery(id+"F0.wireOp",EDGE,"E25.7");var subQ1=sQuery(id+"F0.wireOp",EDGE,"E25.1");var subQ2=sQuery(id+"F0.wireOp",EDGE,"E25.6");var subQ3=sQuery(id+"F0.wireOp",EDGE,"E25.5");var subQ4=sQuery(id+"F0.wireOp",EDGE,"E25.4");var subQ5=sQuery(id+"F0.wireOp",EDGE,"E25.0");var subQ6=sQuery(id+"F0.wireOp",EDGE,"E25.2");var subQ7=sQuery(id+"F0.wireOp",EDGE,"E25.3");Q4=makeQuery(id+"F8.boolean.opBoolean","INTERSECT",EDGE,{"derivedFrom":[makeQuery(id+"F5.boolean.opBoolean","SPLIT",FACE,{"disambiguationData":[TD([makeQuery(id+"F2.opExtrude","SWEPT_FACE",FACE,{"disambiguationData":[OSD([subQ5])]})])],"derivedFrom":makeQuery(id+"F3.boolean.opBoolean","COPY",FACE,{"derivedFrom":makeQuery(id+"F3.opExtrude","CAP_FACE",FACE,{"disambiguationData":[OSD([subQ5,subQ1,subQ6,subQ7,subQ4,subQ3,subQ2,subQ0])],"isStart":false})})}),makeQuery(id+"F8.opExtrude","SWEPT_FACE",FACE,{"disambiguationData":[OSD([sQuery(id+"F7.wireOp",EDGE,"E67")])]})]});}
            var Q5;
            Q5=makeQuery(id+"F8.boolean.opBoolean","INTERSECT",EDGE,{"disambiguationData":[OD(0.0)],"derivedFrom":[makeQuery(id+"F5.opExtrude","SWEPT_FACE",FACE,{"disambiguationData":[OSD([sQuery(id+"F4.wireOp",EDGE,"E30")])]}),makeQuery(id+"F8.opExtrude","SWEPT_FACE",FACE,{"disambiguationData":[OSD([sQuery(id+"F7.wireOp",EDGE,"E67")])]})]});
            fillet(context, id + "F14", {"entities" : qUnion([Q0, Q1, Q2, Q3, Q4, Q5]), "radius" : 3 * mm, "tangentPropagation" : true, "allowEdgeOverflow" : false});
        }
        {
            var Q0;
            Q0=makeQuery(id+"F1.opExtrude","CAP_EDGE",EDGE,{"disambiguationData":[OSD([sQuery(id+"F0.wireOp",EDGE,"E1.bottom")])],"isStart":false});
            fillet(context, id + "F15", {"entities" : qUnion([Q0]), "radius" : 2 * mm, "tangentPropagation" : true, "allowEdgeOverflow" : false});
        }
        {
            var Q0;
            {var subQ0=sQuery(id+"F0.wireOp",EDGE,"E21.filletArc");var subQ1=sQuery(id+"F0.wireOp",EDGE,"E7");var subQ2=sQuery(id+"F0.wireOp",EDGE,"E6");var subQ3=sQuery(id+"F0.wireOp",EDGE,"E5");var subQ4=sQuery(id+"F0.wireOp",EDGE,"E4");var subQ5=sQuery(id+"F0.wireOp",EDGE,"E22.filletArc");var subQ6=sQuery(id+"F0.wireOp",EDGE,"E1.bottom");var subQ7=sQuery(id+"F0.wireOp",EDGE,"E1.right");var subQ8=sQuery(id+"F0.wireOp",EDGE,"E1.top");var subQ9=sQuery(id+"F0.wireOp",EDGE,"E1.left");var subQ10=sQuery(id+"F0.wireOp",EDGE,"E23.filletArc");var subQ11=sQuery(id+"F0.wireOp",EDGE,"E24.filletArc");Q0=makeQuery(id+"F2.boolean.opBoolean","SPLIT",FACE,{"disambiguationData":[TD([makeQuery(id+"F1.opExtrude","SWEPT_FACE",FACE,{"disambiguationData":[OSD([subQ6])]})])],"derivedFrom":makeQuery(id+"F1.opExtrude","CAP_FACE",FACE,{"disambiguationData":[OSD([subQ6,subQ8,subQ9,subQ7,subQ4,subQ3,subQ2,subQ1,subQ0,subQ5,subQ10,subQ11])],"isStart":true})});}
            var sketch = newSketch(context, id + "F16", { "sketchPlane" : qUnion([Q0])});
            skLineSegment(sketch, "E79", {"start": v(0, 74.25) * mm, "end": v(0, 104.25) * mm, "construction": true});
            skCircle(sketch, "E80", {"center": v(0, 104.25) * mm, "radius": 6 * mm});
            skArc(sketch, "E81", {"start": v(15.52, 107.59) * mm, "mid": v(0.98, 118.48) * mm, "end": v(-13.4, 107.38) * mm});
            skLineSegment(sketch, "E82", {"start": v(-13.4, 107.38) * mm, "end": v(-13.4, 92.25) * mm});
            skLineSegment(sketch, "E83", {"start": v(15.52, 107.59) * mm, "end": v(15.52, 90.35) * mm});
            skLineSegment(sketch, "E84", {"start": v(-13.4, 92.25) * mm, "end": v(-31.4, 74.25) * mm});
            skLineSegment(sketch, "E85", {"start": v(15.52, 90.35) * mm, "end": v(31.62, 74.25) * mm});
            skLineSegment(sketch, "E86", {"start": v(-74.25, 0) * mm, "end": v(74.25, 0) * mm, "construction": true});
            skLineSegment(sketch, "E87", {"start": v(74.25, 0) * mm, "end": v(65.47, 0) * mm});
            skLineSegment(sketch, "E88.MirrorCS", {"start": v(0, -74.25) * mm, "end": v(0, -104.25) * mm, "construction": true});
            skLineSegment(sketch, "E89.MirrorCS", {"start": v(15.52, -90.35) * mm, "end": v(31.62, -74.25) * mm});
            skLineSegment(sketch, "E90.MirrorCS", {"start": v(-13.4, -92.25) * mm, "end": v(-31.4, -74.25) * mm});
            skLineSegment(sketch, "E91.MirrorCS", {"start": v(15.52, -107.59) * mm, "end": v(15.52, -90.35) * mm});
            skLineSegment(sketch, "E92.MirrorCS", {"start": v(-13.4, -107.38) * mm, "end": v(-13.4, -92.25) * mm});
            skArc(sketch, "E93.MirrorCS", {"start": v(15.52, -107.59) * mm, "mid": v(0.98, -118.48) * mm, "end": v(-13.4, -107.38) * mm});
            skCircle(sketch, "E94.MirrorC", {"center": v(0, -104.25) * mm, "radius": 6 * mm});
            skSolve(sketch);
        }
        {
            var Q0;
            Q0=makeQuery(id+"F16.imprint","IMPRINT",FACE,{"disambiguationData":[TD([[makeQuery(id+"F16.imprint","IMPRINT",EDGE,{"derivedFrom":sQuery(id+"F16.wireOp",EDGE,"E80")}),-1.0]])]});
            var Q1;
            Q1=makeQuery(id+"F16.imprint","IMPRINT",FACE,{"disambiguationData":[TD([[makeQuery(id+"F16.imprint","IMPRINT",EDGE,{"derivedFrom":makeQuery(id+"F1.opExtrude","CAP_EDGE",EDGE,{"disambiguationData":[OSD([sQuery(id+"F0.wireOp",EDGE,"E1.left")])],"isStart":true})}),-1.0]])]});
            var Q2;
            Q2=makeQuery(id+"F16.imprint","IMPRINT",FACE,{"disambiguationData":[TD([[makeQuery(id+"F16.imprint","IMPRINT",EDGE,{"derivedFrom":sQuery(id+"F16.wireOp",EDGE,"E92.MirrorCS")}),-1.0]])]});
            var Q3;
            Q3=makeQuery(id+"F2.opExtrude","CAP_FACE",FACE,{"disambiguationData":[OSD([sQuery(id+"F0.wireOp",EDGE,"E12"),sQuery(id+"F0.wireOp",EDGE,"E13"),sQuery(id+"F0.wireOp",EDGE,"E14"),sQuery(id+"F0.wireOp",EDGE,"E15"),sQuery(id+"F0.wireOp",EDGE,"E17.filletArc"),sQuery(id+"F0.wireOp",EDGE,"E18.filletArc"),sQuery(id+"F0.wireOp",EDGE,"E19.filletArc"),sQuery(id+"F0.wireOp",EDGE,"E20.filletArc"),sQuery(id+"F0.wireOp",EDGE,"E25.0"),sQuery(id+"F0.wireOp",EDGE,"E25.1"),sQuery(id+"F0.wireOp",EDGE,"E25.2"),sQuery(id+"F0.wireOp",EDGE,"E25.3"),sQuery(id+"F0.wireOp",EDGE,"E25.4"),sQuery(id+"F0.wireOp",EDGE,"E25.5"),sQuery(id+"F0.wireOp",EDGE,"E25.6"),sQuery(id+"F0.wireOp",EDGE,"E25.7")])],"isStart":false});
            extrude(context, id + "F17", {"entities" : qUnion([Q0, Q1, Q2]), "endBound" : BoundingType.UP_TO_SURFACE, "endBoundEntityFace" : qUnion([Q3]), "depth" : 25 * mm});
        }
    });
